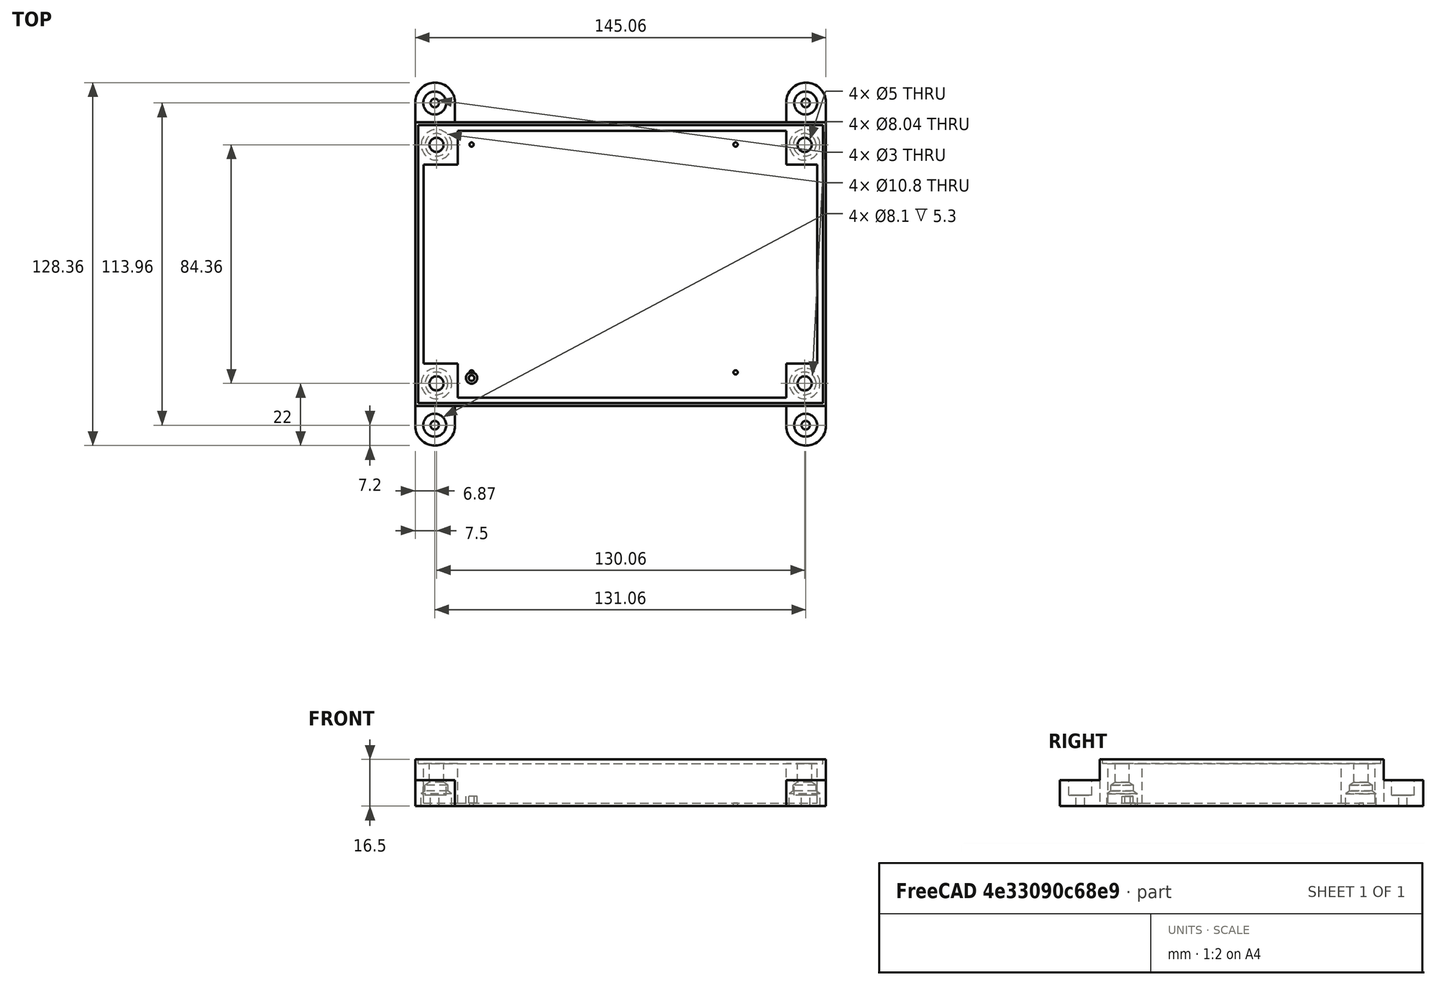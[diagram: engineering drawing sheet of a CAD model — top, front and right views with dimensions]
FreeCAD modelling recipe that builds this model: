
FCSTD DOCUMENT  (FreeCAD 0.16R6712 (Git))
Label: bottom_case_forprinting_sticks
License: All rights reserved
LicenseURL: http://en.wikipedia.org/wiki/All_rights_reserved
objects: Part::FeaturePython×32, Part::Cylinder×25, Part::Cut×23, Part::MultiFuse×21, Part::Box×14, Part::Cone×7, App::MeasureDistance×3, Part::Feature×1, Mesh::Feature×1
note: 123 computed .brp shape members not serialized (recipe doc carries the construction recipe); baked Part::Feature solids carry a one-line shape summary decoded from their .brp

FEATURE [Part::Box] Box  label="bottom_case_master"
  Height = 15
  Length = 145.06
  Placement = pos=(-4,0,0) rot=(0,0,1;0rad)
  Width = 100.36
FEATURE [Part::Box] Box002  label="bottom_case_master_emptying"
  Height = 12
  Length = 118.06
  Placement = pos=(9,3,3) rot=(0,0,1;0rad)
  Width = 94.36
FEATURE [Part::Cut] Cut  label="bottom_case_empty"
  Base = -> Box
  Tool = -> Box002
FEATURE [Part::Box] Box003  label="bottom_case_support_master"
  Height = 9
  Length = 7
  Placement = pos=(18.5,0,0) rot=(0,0,1;0rad)
  Width = 10
FEATURE [Part::FeaturePython] Array  label="array_bottom_case_support_master"  # Draft array (typed FeaturePython)
  Angle = 360
  ArrayType = 0
  Axis = (0,0,1)
  Base = -> Box003
  Center = (0,0,0)
  Fuse = false
  IntervalAxis = (0,0,0)
  IntervalX = (77.06,0,0)
  IntervalY = (0,90.36,0)
  IntervalZ = (0,0,0)
  NumberPolar = 1
  NumberX = 2
  NumberY = 2
  NumberZ = 1
FEATURE [Part::MultiFuse] Fusion
  Shapes = -> [Cut,Array]
FEATURE [Part::Box] Box004  label="correcting_PCB_support"
  Height = 15
  Length = 11
  Width = 98
FEATURE [Part::MultiFuse] Fusion001
  Shapes = -> [Fusion,Box004]
FEATURE [Part::Cylinder] Cylinder
  Angle = 360
  Height = 40
  Placement = pos=(3.5,14,-16) rot=(0,0,1;0rad)
  Radius = 1.75
FEATURE [Part::Cone] Cone
  Angle = 360
  Height = 3
  Placement = pos=(3.5,14,1) rot=(0,0,1;0rad)
  Radius1 = 4.5
  Radius2 = 1.75
FEATURE [Part::MultiFuse] Fusion002
  Shapes = -> [Cylinder,Cone]
FEATURE [Part::Cylinder] Cylinder001
  Angle = 360
  Height = 1
  Placement = pos=(3.5,14,0) rot=(0,0,1;0rad)
  Radius = 4.5
FEATURE [Part::MultiFuse] Fusion003
  Placement = pos=(0,-6,0) rot=(0,0,1;0rad)
  Shapes = -> [Cylinder001,Fusion002]
FEATURE [Part::FeaturePython] Array001  label="array_holes_bottom_case"  # Draft array (typed FeaturePython)
  Angle = 360
  ArrayType = 0
  Axis = (0,0,1)
  Base = -> Fusion003
  Center = (0,0,0)
  Fuse = false
  IntervalAxis = (0,0,0)
  IntervalX = (130.06,0,0)
  IntervalY = (0,84.36,0)
  IntervalZ = (0,0,0)
  NumberPolar = 1
  NumberX = 2
  NumberY = 2
  NumberZ = 1
FEATURE [Part::Cut] Cut001  label="bottom_case"
  Base = -> Fusion001
  Tool = -> Array001
FEATURE [Part::Box] Box008  label="cierre_bottom_length_master"
  Height = 2.5
  Length = 145.06
  Placement = pos=(-4,0,14) rot=(0,0,1;0rad)
  Width = 1
FEATURE [Part::Box] Box009  label="cierre_bottom_width_master"
  Height = 2.5
  Length = 1
  Placement = pos=(-4,0,14) rot=(0,0,1;0rad)
  Width = 100.36
FEATURE [Part::FeaturePython] Array004  label="array_cierre_bottom_length"  # Draft array (typed FeaturePython)
  Angle = 360
  ArrayType = 0
  Axis = (0,0,1)
  Base = -> Box008
  Center = (0,0,0)
  Fuse = false
  IntervalAxis = (0,0,0)
  IntervalX = (1,0,0)
  IntervalY = (0,99.36,0)
  IntervalZ = (0,0,0)
  NumberPolar = 1
  NumberX = 1
  NumberY = 2
  NumberZ = 1
FEATURE [Part::FeaturePython] Array005  label="array_cierre_bottom_width"  # Draft array (typed FeaturePython)
  Angle = 360
  ArrayType = 0
  Axis = (0,0,1)
  Base = -> Box009
  Center = (0,0,0)
  Fuse = false
  IntervalAxis = (0,0,0)
  IntervalX = (144.06,0,0)
  IntervalY = (0,1,0)
  IntervalZ = (0,0,0)
  NumberPolar = 1
  NumberX = 2
  NumberY = 1
  NumberZ = 1
FEATURE [Part::MultiFuse] Fusion005
  Shapes = -> [Array004,Cut001]
FEATURE [Part::MultiFuse] Fusion006  label="bottom_case_with_border"
  Shapes = -> [Array005,Fusion005]
FEATURE [Part::Cylinder] Cylinder011  label="cyl_fix1"
  Angle = 360
  Height = 9.2
  Placement = pos=(3,-5,0) rot=(0,0,1;0rad)
  Radius = 7
FEATURE [Part::Cylinder] Cylinder012  label="cyl_fix2"
  Angle = 360
  Height = 9.2
  Placement = pos=(3,105.36,0) rot=(0,0,1;0rad)
  Radius = 7
FEATURE [Part::Box] Box014  label="cube_fix1"
  Height = 9.2
  Length = 14
  Placement = pos=(-4,-5,0) rot=(0,0,1;0rad)
  Width = 7
FEATURE [Part::MultiFuse] Fusion010  label="fix1_master"
  Shapes = -> [Cylinder011,Box014]
FEATURE [Part::Box] Box015  label="cube_fix2"
  Height = 9.2
  Length = 14
  Placement = pos=(-4,98.36,0) rot=(0,0,1;0rad)
  Width = 7
FEATURE [Part::MultiFuse] Fusion011  label="fix2_master"
  Shapes = -> [Cylinder012,Box015]
FEATURE [Part::FeaturePython] Array010  label="array_fix2"  # Draft array (typed FeaturePython)
  Angle = 360
  ArrayType = 0
  Axis = (0,0,1)
  Base = -> Fusion011
  Center = (0,0,0)
  Fuse = false
  IntervalAxis = (0,0,0)
  IntervalX = (131.06,0,0)
  IntervalY = (0,1,0)
  IntervalZ = (0,0,0)
  NumberPolar = 1
  NumberX = 2
  NumberY = 1
  NumberZ = 1
FEATURE [Part::FeaturePython] Array011  label="array_fix1"  # Draft array (typed FeaturePython)
  Angle = 360
  ArrayType = 0
  Axis = (0,0,1)
  Base = -> Fusion010
  Center = (0,0,0)
  Fuse = false
  IntervalAxis = (0,0,0)
  IntervalX = (131.06,0,0)
  IntervalY = (0,1,0)
  IntervalZ = (0,0,0)
  NumberPolar = 1
  NumberX = 2
  NumberY = 1
  NumberZ = 1
FEATURE [Part::MultiFuse] Fusion012  label="bottom_case_fasterners"
  Shapes = -> [Fusion006,Array010,Array011]
FEATURE [Part::Cylinder] Cylinder013  label="cyl_hole_fastern_master"
  Angle = 360
  Height = 10
  Placement = pos=(2.87,-4.8,-2) rot=(0,0,1;0rad)
  Radius = 1.25
FEATURE [Part::FeaturePython] Array013  label="array_cyl_hole_fastern"  # Draft array (typed FeaturePython)
  Angle = 360
  ArrayType = 0
  Axis = (0,0,1)
  Base = -> Cylinder013
  Center = (0,0,0)
  Fuse = false
  IntervalAxis = (0,0,0)
  IntervalX = (131.06,0,0)
  IntervalY = (0,110.36,0)
  IntervalZ = (0,0,0)
  NumberPolar = 1
  NumberX = 2
  NumberY = 2
  NumberZ = 1
FEATURE [Part::Cut] Cut012  label="bottom_case_hole_fastener_1"
  Base = -> Fusion012
  Tool = -> Array013
FEATURE [Part::Cone] Cone001  label="cone_hole_fastern_master"
  Angle = 360
  Height = 1.8
  Placement = pos=(2.87,-4.8,2.98) rot=(0,0,1;0rad)
  Radius1 = 1.25
  Radius2 = 2.9
FEATURE [Part::FeaturePython] Array014  label="array_cone_hole_fastern"  # Draft array (typed FeaturePython)
  Angle = 360
  ArrayType = 0
  Axis = (0,0,1)
  Base = -> Cone001
  Center = (0,0,0)
  Fuse = false
  IntervalAxis = (0,0,0)
  IntervalX = (131.06,0,0)
  IntervalY = (0,110.36,0)
  IntervalZ = (0,0,0)
  NumberPolar = 1
  NumberX = 2
  NumberY = 2
  NumberZ = 1
FEATURE [Part::Cylinder] Cylinder014  label="cyl_hole_fastern_master001"
  Angle = 360
  Height = 4
  Placement = pos=(2.87,-4.8,6.48) rot=(0,0,1;0rad)
  Radius = 2.2
FEATURE [Part::Box] Box016  label="erase_supports_bottom"
  Height = 10
  Length = 100
  Placement = pos=(11,3,3) rot=(0,0,1;0rad)
  Width = 94.36
FEATURE [Part::Cylinder] Cylinder016  label="hole_PCB_master002"
  Angle = 360
  Height = 30
  Placement = pos=(15.8956,9.8956,-12) rot=(0,0,1;0rad)
  Radius = 1
FEATURE [Part::FeaturePython] Array017  label="array_holes_PCB_bottom_case"  # Draft array (typed FeaturePython)
  Angle = 360
  ArrayType = 0
  Axis = (0,0,1)
  Base = -> Cylinder016
  Center = (0,0,0)
  Fuse = false
  IntervalAxis = (0,0,0)
  IntervalX = (93.2688,0,0)
  IntervalY = (0,80.5688,0)
  IntervalZ = (0,0,0)
  NumberPolar = 1
  NumberX = 2
  NumberY = 2
  NumberZ = 1
FEATURE [Part::Cylinder] Cylinder017  label="hole_complementary_PCB_master"
  Angle = 360
  Height = 3
  Placement = pos=(15.8956,9.8956,0) rot=(0,0,1;0rad)
  Radius = 3.05
FEATURE [Part::FeaturePython] Array018  label="array_holes_complementary_PCB"  # Draft array (typed FeaturePython)
  Angle = 360
  ArrayType = 0
  Axis = (0,0,1)
  Base = -> Cylinder017
  Center = (0,0,0)
  Fuse = false
  IntervalAxis = (0,0,0)
  IntervalX = (93.2688,0,0)
  IntervalY = (0,80.5688,0)
  IntervalZ = (0,0,0)
  NumberPolar = 1
  NumberX = 2
  NumberY = 2
  NumberZ = 1
FEATURE [Part::FeaturePython] Array015  label="array_cyl_hole_fastern2"  # Draft array (typed FeaturePython)
  Angle = 360
  ArrayType = 0
  Axis = (0,0,1)
  Base = -> Cylinder014
  Center = (0,0,0)
  Fuse = false
  IntervalAxis = (0,0,0)
  IntervalX = (131.06,0,0)
  IntervalY = (0,110.36,0)
  IntervalZ = (0,0,0)
  NumberPolar = 1
  NumberX = 2
  NumberY = 2
  NumberZ = 1
FEATURE [Part::MultiFuse] Fusion013
  Shapes = -> [Array015,Array014]
FEATURE [Part::Cut] Cut013  label="bottom_case_fasterners_holes"
  Base = -> Cut012
  Tool = -> Fusion013
FEATURE [Part::Cut] Cut014  label="bottom_case_no_supports"
  Base = -> Cut013
  Tool = -> Box016
FEATURE [Part::Cut] Cut017
  Base = -> Cut014
  Tool = -> Array017
FEATURE [Part::Cut] Cut018  label="bottom_case_PCBholes"
  Base = -> Cut017
  Tool = -> Array018
FEATURE [Part::Cone] Cone003  label="cone_hole_fastern_master002"
  Angle = 360
  Height = 1.8
  Placement = pos=(2.87,-4.8,2.98) rot=(0,0,1;0rad)
  Radius1 = 1.25
  Radius2 = 2.9
FEATURE [Part::FeaturePython] Array020  label="array_cone_hole_fastern002"  # Draft array (typed FeaturePython)
  Angle = 360
  ArrayType = 0
  Axis = (0,0,1)
  Base = -> Cone003
  Center = (0,0,0)
  Fuse = false
  IntervalAxis = (0,0,0)
  IntervalX = (131.06,0,0)
  IntervalY = (0,110.36,0)
  IntervalZ = (0,0,0)
  NumberPolar = 1
  NumberX = 2
  NumberY = 2
  NumberZ = 1
FEATURE [Part::MultiFuse] Fusion014
  Shapes = -> [Cut018,Array020]
FEATURE [Part::Cylinder] Cylinder018  label="cyl_hole_fastern_master002"
  Angle = 360
  Height = 5.4
  Placement = pos=(2.87,-4.8,3.9) rot=(0,0,1;0rad)
  Radius = 4.05
FEATURE [Part::FeaturePython] Array021  label="array_cyl_hole_fastern003"  # Draft array (typed FeaturePython)
  Angle = 360
  ArrayType = 0
  Axis = (0,0,1)
  Base = -> Cylinder018
  Center = (0,0,0)
  Fuse = false
  IntervalAxis = (0,0,0)
  IntervalX = (131.06,0,0)
  IntervalY = (0,110.36,0)
  IntervalZ = (0,0,0)
  NumberPolar = 1
  NumberX = 2
  NumberY = 2
  NumberZ = 1
FEATURE [Part::Cylinder] Cylinder019  label="cyl_hole_fastern_master003"
  Angle = 360
  Height = 10
  Placement = pos=(2.87,-4.8,-2) rot=(0,0,1;0rad)
  Radius = 2.5
FEATURE [Part::FeaturePython] Array022  label="array_cyl_hole_fastern004"  # Draft array (typed FeaturePython)
  Angle = 360
  ArrayType = 0
  Axis = (0,0,1)
  Base = -> Cylinder019
  Center = (0,0,0)
  Fuse = false
  IntervalAxis = (0,0,0)
  IntervalX = (131.06,0,0)
  IntervalY = (0,110.36,0)
  IntervalZ = (0,0,0)
  NumberPolar = 1
  NumberX = 2
  NumberY = 2
  NumberZ = 1
FEATURE [Part::MultiFuse] Fusion015
  Shapes = -> [Fusion014,Array021]
FEATURE [Part::Cut] Cut019
  Base = -> Fusion015
  Tool = -> Array022
FEATURE [Part::Box] Box019  label="Cube"
  Height = 10
  Length = 12
  Placement = pos=(-2,0,0) rot=(0,0,1;0rad)
  Width = 98
FEATURE [Part::FeaturePython] Array023  # Draft array (typed FeaturePython)
  Angle = 360
  ArrayType = 0
  Axis = (0,0,1)
  Base = -> Box019
  Center = (0,0,0)
  Fuse = false
  IntervalAxis = (0,0,0)
  IntervalX = (130,0,0)
  IntervalY = (0,1,0)
  IntervalZ = (0,0,0)
  NumberPolar = 1
  NumberX = 2
  NumberY = 1
  NumberZ = 1
FEATURE [Part::MultiFuse] Fusion016
  Shapes = -> [Array023,Cut019]
FEATURE [Part::Cylinder] Cylinder020
  Angle = 360
  Height = 40
  Placement = pos=(3.5,8,-16) rot=(0,0,1;0rad)
  Radius = 2.5
FEATURE [Part::FeaturePython] Array024  # Draft array (typed FeaturePython)
  Angle = 360
  ArrayType = 0
  Axis = (0,0,1)
  Base = -> Cylinder020
  Center = (0,0,0)
  Fuse = false
  IntervalAxis = (0,0,0)
  IntervalX = (130.06,0,0)
  IntervalY = (0,84.36,0)
  IntervalZ = (0,0,0)
  NumberPolar = 1
  NumberX = 2
  NumberY = 2
  NumberZ = 1
FEATURE [Part::Cut] Cut020  label="bottom_case001"
  Base = -> Fusion016
  Tool = -> Array024
FEATURE [Part::Cylinder] Cylinder021
  Angle = 360
  Height = 3.8
  Placement = pos=(3.5,8,0) rot=(0,0,1;0rad)
  Radius = 2.15
FEATURE [Part::FeaturePython] Array025  # Draft array (typed FeaturePython)
  Angle = 360
  ArrayType = 0
  Axis = (0,0,1)
  Base = -> Cylinder021
  Center = (0,0,0)
  Fuse = false
  IntervalAxis = (0,0,0)
  IntervalX = (130.06,0,0)
  IntervalY = (0,84.36,0)
  IntervalZ = (0,0,0)
  NumberPolar = 1
  NumberX = 2
  NumberY = 2
  NumberZ = 1
FEATURE [Part::Cut] Cut021
  Base = -> Cut020
  Tool = -> Array025
FEATURE [Part::Cut] Cut022
  Base = -> Cut021
  Tool = -> Array021
FEATURE [Part::Cylinder] Cylinder022
  Angle = 360
  Height = 7.4
  Placement = pos=(3.5,8,0) rot=(0,0,1;0rad)
  Radius = 4.02
FEATURE [Part::FeaturePython] Array026  # Draft array (typed FeaturePython)
  Angle = 360
  ArrayType = 0
  Axis = (0,0,1)
  Base = -> Cylinder022
  Center = (0,0,0)
  Fuse = false
  IntervalAxis = (0,0,0)
  IntervalX = (130.06,0,0)
  IntervalY = (0,84.36,0)
  IntervalZ = (0,0,0)
  NumberPolar = 1
  NumberX = 2
  NumberY = 2
  NumberZ = 1
FEATURE [Part::Cut] Cut023  label="bottom_case_end"
  Base = -> Cut022
  Tool = -> Array026
FEATURE [Part::Cone] Cone004  label="Cone001"
  Angle = 360
  Height = 1
  Placement = pos=(3.5,8,7.4) rot=(0,0,1;0rad)
  Radius1 = 4.02
  Radius2 = 2.5
FEATURE [Part::FeaturePython] Array028  # Draft array (typed FeaturePython)
  Angle = 360
  ArrayType = 0
  Axis = (0,0,1)
  Base = -> Cone004
  Center = (0,0,0)
  Fuse = false
  IntervalAxis = (0,0,0)
  IntervalX = (130.06,0,0)
  IntervalY = (0,84.36,0)
  IntervalZ = (0,0,0)
  NumberPolar = 1
  NumberX = 2
  NumberY = 2
  NumberZ = 1
FEATURE [Part::Cut] Cut025
  Base = -> Cut023
  Tool = -> Array028
FEATURE [Part::Cone] Cone005  label="Cone002"
  Angle = 360
  Height = 0.5
  Placement = pos=(15.8956,9.8956,1.8) rot=(0,0,1;0rad)
  Radius1 = 3.05
  Radius2 = 1
FEATURE [Part::FeaturePython] Array029  # Draft array (typed FeaturePython)
  Angle = 360
  ArrayType = 0
  Axis = (0,0,1)
  Base = -> Cone005
  Center = (0,0,0)
  Fuse = false
  IntervalAxis = (0,0,0)
  IntervalX = (93.2688,0,0)
  IntervalY = (0,80.5688,0)
  IntervalZ = (0,0,0)
  NumberPolar = 1
  NumberX = 2
  NumberY = 2
  NumberZ = 1
FEATURE [Part::Cut] Cut026  label="bottom_case_finished"
  Base = -> Cut025
  Tool = -> Array029
FEATURE [App::MeasureDistance] Distance  label="Distance: 145,06 mm"
  Distance = 145.06
  P1 = (-4,0,16.5)
  P2 = (141.06,0,16.5)
FEATURE [Part::Cylinder] Cylinder023  label="hole_complementary_PCB_master001"
  Angle = 360
  Height = 3
  Placement = pos=(15.8956,9.8956,0) rot=(0,0,1;0rad)
  Radius = 3.05
FEATURE [Part::FeaturePython] Array030  label="array_holes_complementary_PCB001"  # Draft array (typed FeaturePython)
  Angle = 360
  ArrayType = 0
  Axis = (0,0,1)
  Base = -> Cylinder023
  Center = (0,0,0)
  Fuse = false
  IntervalAxis = (0,0,0)
  IntervalX = (93.2688,0,0)
  IntervalY = (0,80.5688,0)
  IntervalZ = (0,0,0)
  NumberPolar = 1
  NumberX = 2
  NumberY = 2
  NumberZ = 1
FEATURE [Part::MultiFuse] Fusion017
  Shapes = -> [Array030,Cut026]
FEATURE [Part::Cylinder] Cylinder024  label="hole_PCB_master003"
  Angle = 360
  Height = 30
  Placement = pos=(15.8956,9.8956,-12) rot=(0,0,1;0rad)
  Radius = 1
FEATURE [Part::FeaturePython] Array031  label="array_holes_PCB_bottom_case001"  # Draft array (typed FeaturePython)
  Angle = 360
  ArrayType = 0
  Axis = (0,0,1)
  Base = -> Cylinder024
  Center = (0,0,0)
  Fuse = false
  IntervalAxis = (0,0,0)
  IntervalX = (93.2688,0,0)
  IntervalY = (0,80.5688,0)
  IntervalZ = (0,0,0)
  NumberPolar = 1
  NumberX = 2
  NumberY = 2
  NumberZ = 1
FEATURE [Part::Cut] Cut027
  Base = -> Fusion017
  Tool = -> Array031
FEATURE [Part::Cylinder] Cylinder025  label="cyl_hole_fastern_master004"
  Angle = 360
  Height = 9
  Placement = pos=(2.87,-6.8,-2) rot=(0,0,1;0rad)
  Radius = 1.5
FEATURE [Part::FeaturePython] Array032  label="array_cyl_hole_fastern005"  # Draft array (typed FeaturePython)
  Angle = 360
  ArrayType = 0
  Axis = (0,0,1)
  Base = -> Cylinder025
  Center = (0,0,0)
  Fuse = false
  IntervalAxis = (0,0,0)
  IntervalX = (131.06,0,0)
  IntervalY = (0,113.96,0)
  IntervalZ = (0,0,0)
  NumberPolar = 1
  NumberX = 2
  NumberY = 2
  NumberZ = 1
FEATURE [Part::Cylinder] Cylinder026  label="cyl_hole_fastern_master005"
  Angle = 360
  Height = 5.4
  Placement = pos=(2.87,-6.8,3.9) rot=(0,0,1;0rad)
  Radius = 4.05
FEATURE [Part::FeaturePython] Array033  label="array_cyl_hole_fastern006"  # Draft array (typed FeaturePython)
  Angle = 360
  ArrayType = 0
  Axis = (0,0,1)
  Base = -> Cylinder026
  Center = (0,0,0)
  Fuse = false
  IntervalAxis = (0,0,0)
  IntervalX = (131.06,0,0)
  IntervalY = (0,113.96,0)
  IntervalZ = (0,0,0)
  NumberPolar = 1
  NumberX = 2
  NumberY = 2
  NumberZ = 1
FEATURE [Part::Cylinder] Cylinder027  label="cyl_fix003"
  Angle = 360
  Height = 9.2
  Placement = pos=(3,107.36,0) rot=(0,0,1;0rad)
  Radius = 7
FEATURE [Part::Box] Box020  label="cube_fix003"
  Height = 9.2
  Length = 14
  Placement = pos=(-4,98.36,0) rot=(0,0,1;0rad)
  Width = 9
FEATURE [Part::MultiFuse] Fusion018  label="fix2_master001"
  Shapes = -> [Cylinder027,Box020]
FEATURE [Part::FeaturePython] Array034  label="array_fix003"  # Draft array (typed FeaturePython)
  Angle = 360
  ArrayType = 0
  Axis = (0,0,1)
  Base = -> Fusion018
  Center = (0,0,0)
  Fuse = false
  IntervalAxis = (0,0,0)
  IntervalX = (131.06,0,0)
  IntervalY = (0,1,0)
  IntervalZ = (0,0,0)
  NumberPolar = 1
  NumberX = 2
  NumberY = 1
  NumberZ = 1
FEATURE [Part::Cylinder] Cylinder028  label="cyl_fix004"
  Angle = 360
  Height = 9.2
  Placement = pos=(3,-7,0) rot=(0,0,1;0rad)
  Radius = 7
FEATURE [Part::Box] Box021  label="cube_fix004"
  Height = 9.2
  Length = 14
  Placement = pos=(-4,-7,0) rot=(0,0,1;0rad)
  Width = 9
FEATURE [Part::MultiFuse] Fusion019  label="fix1_master001"
  Shapes = -> [Cylinder028,Box021]
FEATURE [Part::FeaturePython] Array035  label="array_fix004"  # Draft array (typed FeaturePython)
  Angle = 360
  ArrayType = 0
  Axis = (0,0,1)
  Base = -> Fusion019
  Center = (0,0,0)
  Fuse = false
  IntervalAxis = (0,0,0)
  IntervalX = (131.06,0,0)
  IntervalY = (0,1,0)
  IntervalZ = (0,0,0)
  NumberPolar = 1
  NumberX = 2
  NumberY = 1
  NumberZ = 1
FEATURE [Part::MultiFuse] Fusion020
  Shapes = -> [Array034,Cut027]
FEATURE [Part::MultiFuse] Fusion021
  Shapes = -> [Array035,Fusion020]
FEATURE [App::MeasureDistance] Distance001  label="Distance: 17,9618 mm"
  Distance = 17.9618
  P1 = (133.812,96.3721,0)
  P2 = (133.861,114.334,0)
FEATURE [App::MeasureDistance] Distance002  label="Distance: 17,9422 mm"
  Distance = 17.9422
  P1 = (133.811,3.98801,0)
  P2 = (134.512,-13.9405,0)
FEATURE [Part::Cut] Cut028
  Base = -> Fusion021
  Tool = -> Array033
FEATURE [Part::Cut] Cut029
  Base = -> Cut028
  Tool = -> Array032
FEATURE [Part::Box] Box022  label="Cube001"
  Height = 10
  Length = 116.06
  Placement = pos=(11,3,1) rot=(0,0,1;0rad)
  Width = 94.36
FEATURE [Part::Cut] Cut030  label="bottom_case_holes"
  Base = -> Cut029
  Tool = -> Box022
FEATURE [Part::Cylinder] Cylinder029  label="hole_PCB_master004"
  Angle = 360
  Height = 1
  Placement = pos=(15.8956,9.8956,0) rot=(0,0,1;0rad)
  Radius = 1
FEATURE [Part::FeaturePython] Array036  label="array_holes_PCB_bottom_case002"  # Draft array (typed FeaturePython)
  Angle = 360
  ArrayType = 0
  Axis = (0,0,1)
  Base = -> Cylinder029
  Center = (0,0,0)
  Fuse = false
  IntervalAxis = (0,0,0)
  IntervalX = (93.2688,0,0)
  IntervalY = (0,80.5688,0)
  IntervalZ = (0,0,0)
  NumberPolar = 1
  NumberX = 2
  NumberY = 2
  NumberZ = 1
FEATURE [Part::Cylinder] Cylinder030  label="hole_PCB_master005"
  Angle = 360
  Height = 14
  Placement = pos=(15.8956,11.8956,0) rot=(0,0,1;0rad)
  Radius = 0.75
FEATURE [Part::FeaturePython] Array037  label="array_holes_PCB_bottom_case003"  # Draft array (typed FeaturePython)
  Angle = 360
  ArrayType = 0
  Axis = (0,0,1)
  Base = -> Cylinder030
  Center = (0,0,0)
  Fuse = false
  IntervalAxis = (0,0,0)
  IntervalX = (93.2688,0,0)
  IntervalY = (0,80.5688,0)
  IntervalZ = (0,0,0)
  NumberPolar = 1
  NumberX = 2
  NumberY = 2
  NumberZ = 1
FEATURE [Part::MultiFuse] Fusion022
  Shapes = -> [Array036,Cut030]
FEATURE [Part::Cylinder] Cylinder031  label="hole_PCB_master006"
  Angle = 360
  Height = 2.5
  Placement = pos=(15.8956,9.8956,0) rot=(0,0,1;0rad)
  Radius = 2
FEATURE [Part::MultiFuse] Fusion023  label="bottom_case_sticks"
  Shapes = -> [Array037,Fusion022]
FEATURE [Part::Cylinder] Cylinder032  label="hole_PCB_master007"
  Angle = 360
  Height = 2.5
  Placement = pos=(15.8956,9.8956,0) rot=(0,0,1;0rad)
  Radius = 1
FEATURE [Part::Cut] Cut031  label="pcb_support"
  Base = -> Cylinder031
  Placement = pos=(0,0,1) rot=(0,0,1;0rad)
  Tool = -> Cylinder032
FEATURE [Part::Cone] Cone006  label="Cone003"
  Angle = 360
  Height = 2
  Placement = pos=(15.8956,11.8956,14) rot=(0,0,1;0rad)
  Radius1 = 0.75
  Radius2 = 0.1
FEATURE [Part::FeaturePython] Array038  label="cones_sticks"  # Draft array (typed FeaturePython)
  Angle = 360
  ArrayType = 0
  Axis = (0,0,1)
  Base = -> Cone006
  Center = (0,0,0)
  Fuse = false
  IntervalAxis = (0,0,0)
  IntervalX = (93.2688,0,0)
  IntervalY = (0,80.5688,0)
  IntervalZ = (0,0,0)
  NumberPolar = 1
  NumberX = 2
  NumberY = 2
  NumberZ = 1
FEATURE [Part::MultiFuse] Fusion024  label="bottom_case_sticks001"
  Shapes = -> [Array038,Fusion023]
FEATURE [Part::Cone] Cone007  label="Cone004"
  Angle = 360
  Height = 1
  Placement = pos=(3.5,8,4.4) rot=(0,0,1;0rad)
  Radius1 = 5.4
  Radius2 = 4.02
FEATURE [Part::FeaturePython] Array039  # Draft array (typed FeaturePython)
  Angle = 360
  ArrayType = 0
  Axis = (0,0,1)
  Base = -> Cone007
  Center = (0,0,0)
  Fuse = false
  IntervalAxis = (0,0,0)
  IntervalX = (130.06,0,0)
  IntervalY = (0,84.36,0)
  IntervalZ = (0,0,0)
  NumberPolar = 1
  NumberX = 2
  NumberY = 2
  NumberZ = 1
FEATURE [Part::Cylinder] Cylinder033
  Angle = 360
  Height = 7.4
  Placement = pos=(3.5,8,-3) rot=(0,0,1;0rad)
  Radius = 5.4
FEATURE [Part::FeaturePython] Array040  # Draft array (typed FeaturePython)
  Angle = 360
  ArrayType = 0
  Axis = (0,0,1)
  Base = -> Cylinder033
  Center = (0,0,0)
  Fuse = false
  IntervalAxis = (0,0,0)
  IntervalX = (130.06,0,0)
  IntervalY = (0,84.36,0)
  IntervalZ = (0,0,0)
  NumberPolar = 1
  NumberX = 2
  NumberY = 2
  NumberZ = 1
FEATURE [Part::Cut] Cut032
  Base = -> Fusion024
  Tool = -> Array039
FEATURE [Part::Cut] Cut033  label="bottom_case_sticks_v2"
  Base = -> Cut032
  Tool = -> Array040
FEATURE [Part::Box] Box023  label="Cube002"
  Height = 16
  Length = 139.06
  Placement = pos=(-1,15,1) rot=(0,0,1;0rad)
  Width = 70.36
FEATURE [Part::Cut] Cut034  label="bottom_case_def"
  Base = -> Cut033
  Tool = -> Box023
FEATURE [Part::Cylinder] Cylinder034  label="hole_PCB_master008"
  Angle = 360
  Height = 23
  Placement = pos=(15.8956,11.8956,-6) rot=(0,0,1;0rad)
  Radius = 0.75
FEATURE [Part::FeaturePython] Array041  label="array_holes_PCB_bottom_case004"  # Draft array (typed FeaturePython)
  Angle = 360
  ArrayType = 0
  Axis = (0,0,1)
  Base = -> Cylinder034
  Center = (0,0,0)
  Fuse = false
  IntervalAxis = (0,0,0)
  IntervalX = (93.2688,0,0)
  IntervalY = (0,80.5688,0)
  IntervalZ = (0,0,0)
  NumberPolar = 1
  NumberX = 2
  NumberY = 2
  NumberZ = 1
FEATURE [Part::Cut] Cut035
  Base = -> Cut034
  Tool = -> Array041
FEATURE [Part::Feature] Cut035_solid  label="Cut035 (Solid)"
  shape: bbox 145.1 x 128.4 x 16.5 mm, 72 faces (baked)
FEATURE [Mesh::Feature] Mesh  label="Cut035 (Solid) (Meshed)"
